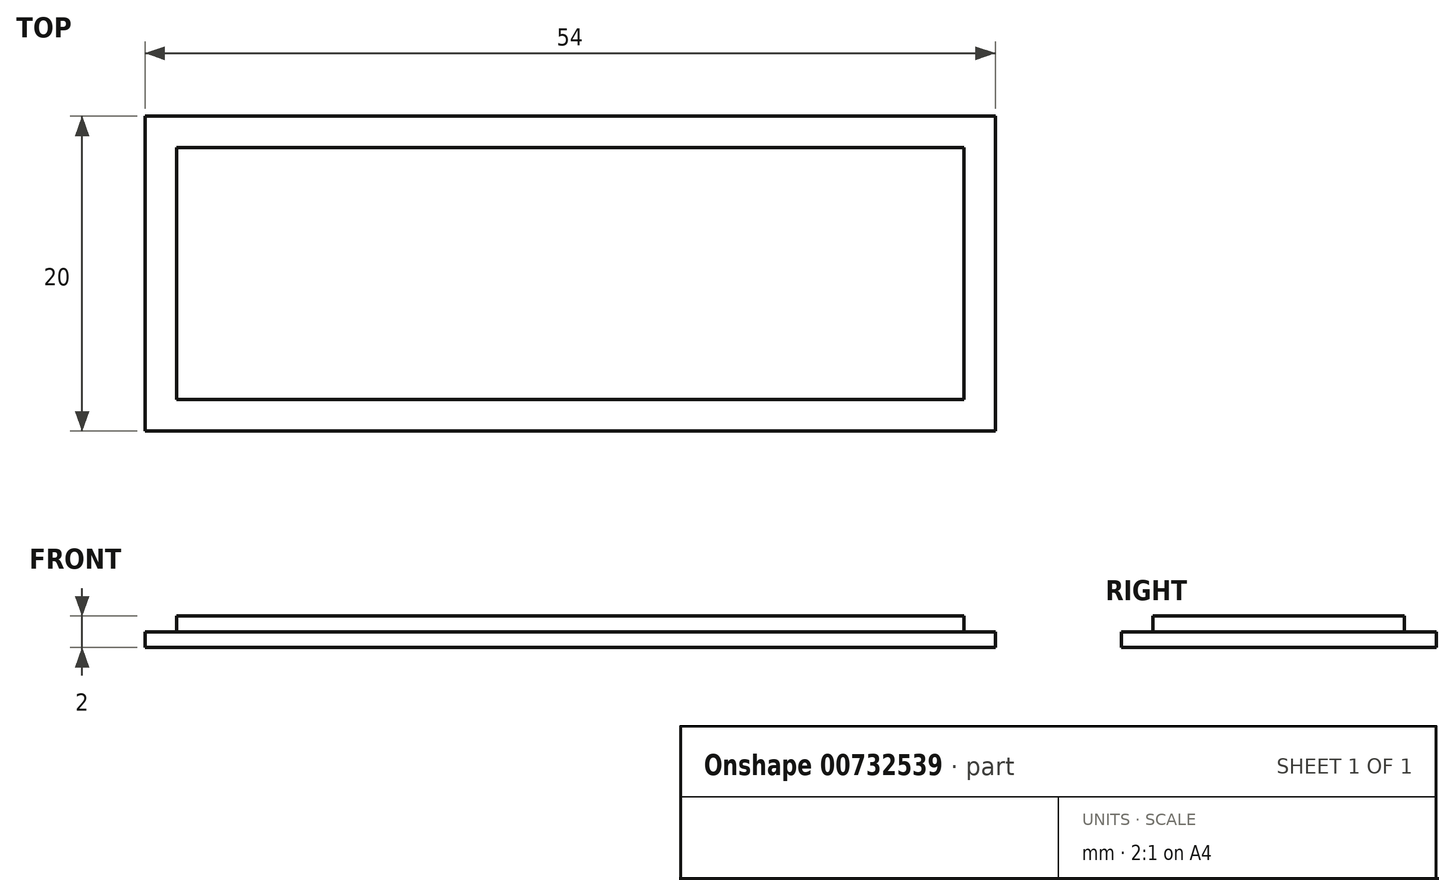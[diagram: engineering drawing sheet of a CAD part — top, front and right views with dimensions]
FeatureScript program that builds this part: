
annotation { "Feature Type Name" : "Feature", "Feature Type Description" : "" }
export const myFeature = defineFeature(function(context is Context, id is Id, definition is map)
    precondition{}
    {
        {
            var Q0;
            Q0=qCreatedBy(makeId("Top.planeOp"),FACE);
            var sketch = newSketch(context, id + "F0", { "sketchPlane" : qUnion([Q0])});
            skLineSegment(sketch, "E0.bottom", {"start": v(27, 10) * mm, "end": v(-27, 10) * mm});
            skLineSegment(sketch, "E0.top", {"start": v(27, -10) * mm, "end": v(-27, -10) * mm});
            skLineSegment(sketch, "E0.left", {"start": v(27, 10) * mm, "end": v(27, -10) * mm});
            skLineSegment(sketch, "E0.right", {"start": v(-27, 10) * mm, "end": v(-27, -10) * mm});
            skPoint(sketch, "E0.middle", {"position": v(0, 0) * mm});
            skSolve(sketch);
        }
        {
            var Q0;
            Q0=makeQuery(id+"F0.imprint","IMPRINT",FACE,{"disambiguationData":[TD([[makeQuery(id+"F0.imprint","IMPRINT",EDGE,{"derivedFrom":sQuery(id+"F0.wireOp",EDGE,"E0.bottom")}),1.0]])]});
            extrude(context, id + "F1", {"entities" : qUnion([Q0]), "depth" : 1 * mm, "offsetDistance" : 25 * mm});
        }
        {
            var Q0;
            Q0=makeQuery(id+"F1.opExtrude","CAP_FACE",FACE,{"disambiguationData":[OSD([sQuery(id+"F0.wireOp",EDGE,"E0.bottom"),sQuery(id+"F0.wireOp",EDGE,"E0.top"),sQuery(id+"F0.wireOp",EDGE,"E0.left"),sQuery(id+"F0.wireOp",EDGE,"E0.right")])],"isStart":false});
            var sketch = newSketch(context, id + "F2", { "sketchPlane" : qUnion([Q0])});
            skLineSegment(sketch, "E1.bottom", {"start": v(25, -8) * mm, "end": v(-25, -8) * mm});
            skLineSegment(sketch, "E1.top", {"start": v(25, 8) * mm, "end": v(-25, 8) * mm});
            skLineSegment(sketch, "E1.left", {"start": v(25, -8) * mm, "end": v(25, 8) * mm});
            skLineSegment(sketch, "E1.right", {"start": v(-25, -8) * mm, "end": v(-25, 8) * mm});
            skPoint(sketch, "E1.middle", {"position": v(0, 0) * mm});
            skSolve(sketch);
        }
        {
            var Q0;
            Q0=makeQuery(id+"F2.imprint","IMPRINT",FACE,{"disambiguationData":[TD([[makeQuery(id+"F2.imprint","IMPRINT",EDGE,{"derivedFrom":sQuery(id+"F2.wireOp",EDGE,"E1.bottom")}),-1.0]])]});
            extrude(context, id + "F3", {"entities" : qUnion([Q0]), "depth" : 1 * mm, "offsetDistance" : 25 * mm});
        }
    });
